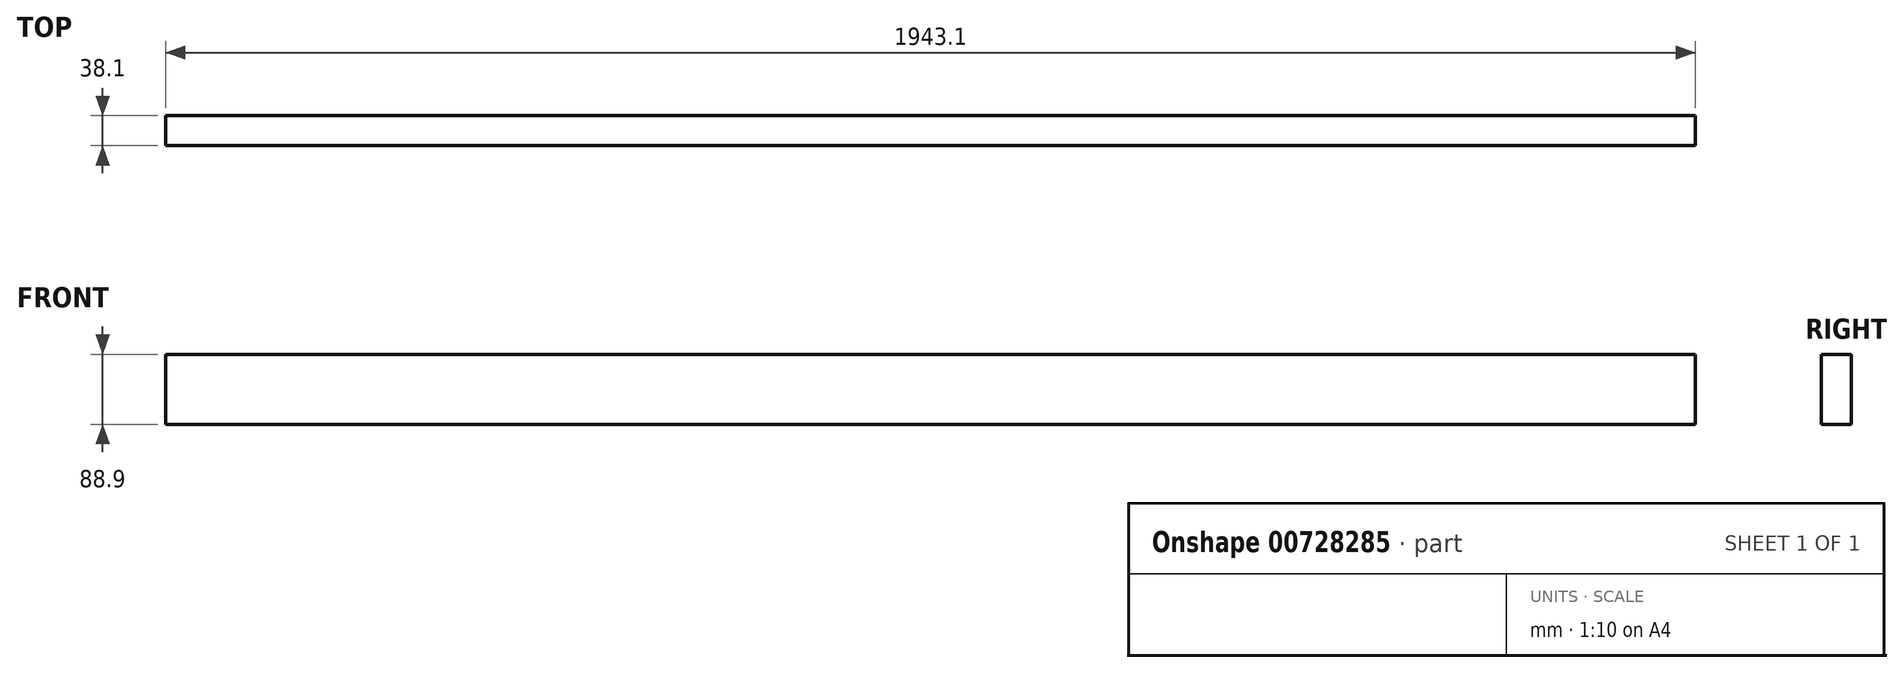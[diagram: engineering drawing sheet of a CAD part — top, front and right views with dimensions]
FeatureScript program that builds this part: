
annotation { "Feature Type Name" : "Feature", "Feature Type Description" : "" }
export const myFeature = defineFeature(function(context is Context, id is Id, definition is map)
    precondition{}
    {
        {
            var Q0;
            Q0=qCreatedBy(makeId("Front.planeOp"),FACE);
            var sketch = newSketch(context, id + "F0", { "sketchPlane" : qUnion([Q0])});
            skLineSegment(sketch, "E0.bottom", {"start": v(-971.55, -44.45) * mm, "end": v(971.55, -44.45) * mm});
            skLineSegment(sketch, "E0.top", {"start": v(-971.55, 44.45) * mm, "end": v(971.55, 44.45) * mm});
            skLineSegment(sketch, "E0.left", {"start": v(-971.55, -44.45) * mm, "end": v(-971.55, 44.45) * mm});
            skLineSegment(sketch, "E0.right", {"start": v(971.55, -44.45) * mm, "end": v(971.55, 44.45) * mm});
            skPoint(sketch, "E0.middle", {"position": v(0, 0) * mm});
            skSolve(sketch);
        }
        {
            var Q0;
            Q0=qSketchRegion(id+"F0",true);
            extrude(context, id + "F1", {"entities" : qUnion([Q0]), "depth" : 38.1 * mm, "offsetDistance" : 25.4 * mm});
        }
    });
